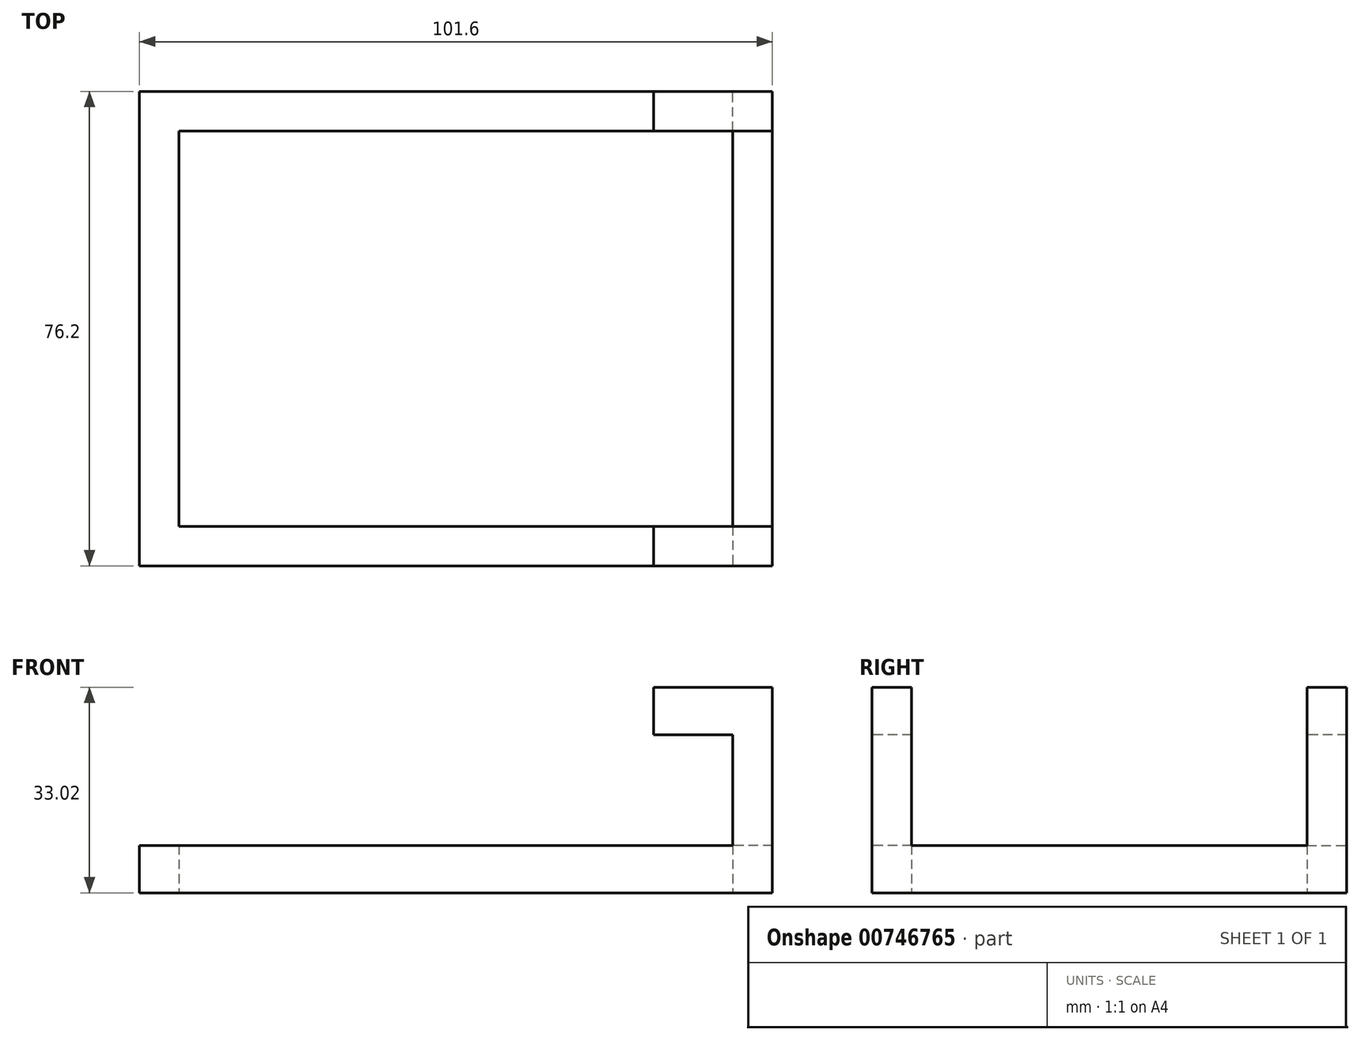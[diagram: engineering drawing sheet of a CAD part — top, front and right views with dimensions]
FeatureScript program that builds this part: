
annotation { "Feature Type Name" : "Feature", "Feature Type Description" : "" }
export const myFeature = defineFeature(function(context is Context, id is Id, definition is map)
    precondition{}
    {
        {
            var Q0;
            Q0=qCreatedBy(makeId("Top.planeOp"),FACE);
            var sketch = newSketch(context, id + "F0", { "sketchPlane" : qUnion([Q0])});
            skLineSegment(sketch, "E0.bottom", {"start": v(-50.8, 38.1) * mm, "end": v(50.8, 38.1) * mm});
            skLineSegment(sketch, "E0.top", {"start": v(-50.8, -38.1) * mm, "end": v(50.8, -38.1) * mm});
            skLineSegment(sketch, "E0.left", {"start": v(-50.8, 38.1) * mm, "end": v(-50.8, -38.1) * mm});
            skLineSegment(sketch, "E0.right", {"start": v(50.8, 38.1) * mm, "end": v(50.8, -38.1) * mm});
            skPoint(sketch, "E0.middle", {"position": v(0, 0) * mm});
            skLineSegment(sketch, "E1.bottom", {"start": v(-44.45, 31.75) * mm, "end": v(44.45, 31.75) * mm});
            skLineSegment(sketch, "E1.top", {"start": v(-44.45, -31.75) * mm, "end": v(44.45, -31.75) * mm});
            skLineSegment(sketch, "E1.left", {"start": v(-44.45, 31.75) * mm, "end": v(-44.45, -31.75) * mm});
            skLineSegment(sketch, "E1.right", {"start": v(44.45, 31.75) * mm, "end": v(44.45, -31.75) * mm});
            skLineSegment(sketch, "E2", {"start": v(50.8, 4.61) * mm, "end": v(50.8, 38.1) * mm});
            skSolve(sketch);
        }
        {
            var Q0;
            {var subQ3=sQuery(id+"F0.wireOp",EDGE,"E0.bottom");Q0=makeQuery(id+"F0.imprint","IMPRINT",FACE,{"disambiguationData":[TD([[makeQuery(id+"F0.imprint","IMPRINT",EDGE,{"derivedFrom":subQ3}),-1.0]])]});}
            extrude(context, id + "F1", {"entities" : qUnion([Q0]), "depth" : 7.62 * mm, "offsetDistance" : 25.4 * mm});
        }
        {
            var Q0;
            Q0=makeQuery(id+"F1.opExtrude","CAP_FACE",FACE,{"disambiguationData":[OSD([sQuery(id+"F0.wireOp",EDGE,"E0.bottom"),sQuery(id+"F0.wireOp",EDGE,"E0.top"),sQuery(id+"F0.wireOp",EDGE,"E0.left"),sQuery(id+"F0.wireOp",EDGE,"E0.right"),sQuery(id+"F0.wireOp",EDGE,"E1.bottom"),sQuery(id+"F0.wireOp",EDGE,"E1.top"),sQuery(id+"F0.wireOp",EDGE,"E1.left"),sQuery(id+"F0.wireOp",EDGE,"E1.right")])],"isStart":false});
            var sketch = newSketch(context, id + "F2", { "sketchPlane" : qUnion([Q0])});
            skLineSegment(sketch, "E3", {"start": v(44.45, -31.75) * mm, "end": v(44.45, -38.1) * mm});
            skLineSegment(sketch, "E4", {"start": v(44.45, -38.1) * mm, "end": v(50.8, -38.1) * mm});
            skLineSegment(sketch, "E5", {"start": v(50.8, -38.1) * mm, "end": v(50.8, -31.75) * mm});
            skLineSegment(sketch, "E6", {"start": v(50.8, -31.75) * mm, "end": v(44.45, -31.75) * mm});
            skLineSegment(sketch, "E7", {"start": v(44.45, 31.75) * mm, "end": v(44.45, 38.1) * mm});
            skLineSegment(sketch, "E8", {"start": v(44.45, 38.1) * mm, "end": v(50.8, 38.1) * mm});
            skLineSegment(sketch, "E9", {"start": v(50.8, 38.1) * mm, "end": v(50.8, 31.75) * mm});
            skLineSegment(sketch, "E10", {"start": v(50.8, 31.75) * mm, "end": v(44.45, 31.75) * mm});
            skSolve(sketch);
        }
        {
            var Q0;
            Q0=makeQuery(id+"F2.imprint","IMPRINT",FACE,{"disambiguationData":[TD([[makeQuery(id+"F2.imprint","IMPRINT",EDGE,{"derivedFrom":sQuery(id+"F2.wireOp",EDGE,"E3")}),1.0]])]});
            var Q1;
            Q1=makeQuery(id+"F2.imprint","IMPRINT",FACE,{"disambiguationData":[TD([[makeQuery(id+"F2.imprint","IMPRINT",EDGE,{"derivedFrom":sQuery(id+"F2.wireOp",EDGE,"E7")}),-1.0]])]});
            extrude(context, id + "F3", {"entities" : qUnion([Q0, Q1]), "operationType" : NewBodyOperationType.ADD, "depth" : 25.4 * mm, "offsetDistance" : 25.4 * mm});
        }
        {
            var Q0;
            Q0=makeQuery(id+"F3.opExtrude","SWEPT_FACE",FACE,{"disambiguationData":[OSD([sQuery(id+"F2.wireOp",EDGE,"E7")])]});
            var sketch = newSketch(context, id + "F4", { "sketchPlane" : qUnion([Q0])});
            skLineSegment(sketch, "E11", {"start": v(-38.1, 33.02) * mm, "end": v(-38.1, 25.4) * mm});
            skLineSegment(sketch, "E12", {"start": v(-38.1, 25.4) * mm, "end": v(-31.75, 25.4) * mm});
            skLineSegment(sketch, "E13", {"start": v(-31.75, 25.4) * mm, "end": v(-31.75, 33.02) * mm});
            skLineSegment(sketch, "E14", {"start": v(-31.75, 33.02) * mm, "end": v(-38.1, 33.02) * mm});
            skSolve(sketch);
        }
        {
            var Q0;
            Q0 = qSketchRegion(id + "F4", true);
            extrude(context, id + "F5", {"entities" : qUnion([Q0]), "operationType" : NewBodyOperationType.ADD, "depth" : 12.7 * mm, "offsetDistance" : 25.4 * mm});
        }
        {
            var Q0;
            Q0=makeQuery(id+"F3.opExtrude","SWEPT_FACE",FACE,{"disambiguationData":[OSD([sQuery(id+"F2.wireOp",EDGE,"E3")])]});
            var sketch = newSketch(context, id + "F6", { "sketchPlane" : qUnion([Q0])});
            skLineSegment(sketch, "E15", {"start": v(31.75, 33.02) * mm, "end": v(31.75, 25.4) * mm});
            skLineSegment(sketch, "E16", {"start": v(31.75, 25.4) * mm, "end": v(38.1, 25.4) * mm});
            skLineSegment(sketch, "E17", {"start": v(38.1, 25.4) * mm, "end": v(38.1, 33.02) * mm});
            skLineSegment(sketch, "E18", {"start": v(38.1, 33.02) * mm, "end": v(31.75, 33.02) * mm});
            skSolve(sketch);
        }
        {
            var Q0;
            Q0 = qSketchRegion(id + "F6", true);
            extrude(context, id + "F7", {"entities" : qUnion([Q0]), "operationType" : NewBodyOperationType.ADD, "depth" : 12.7 * mm, "offsetDistance" : 25.4 * mm});
        }
    });
